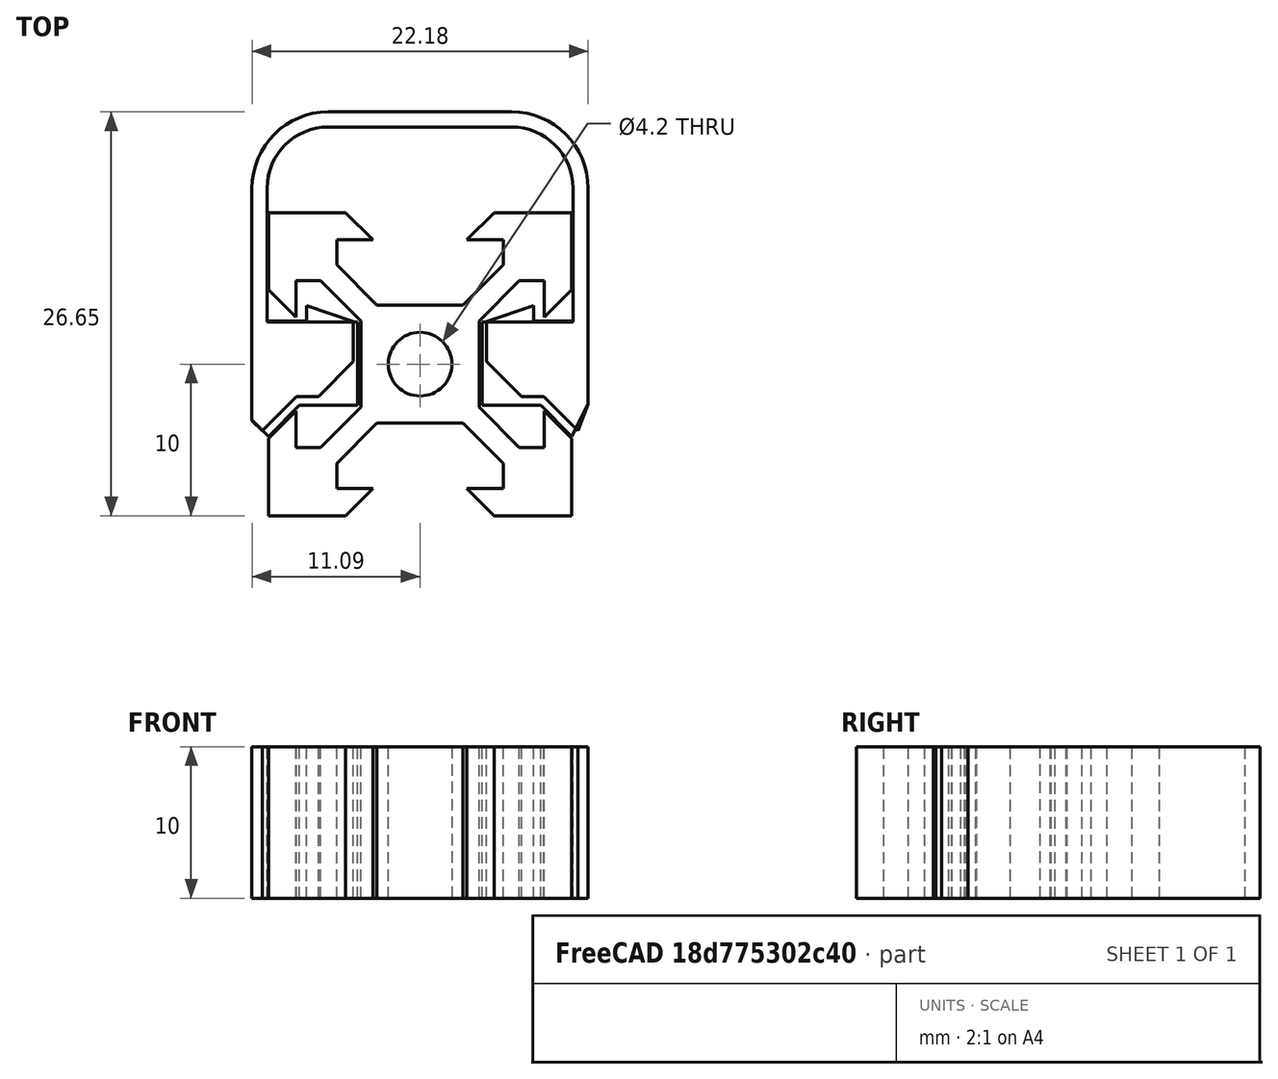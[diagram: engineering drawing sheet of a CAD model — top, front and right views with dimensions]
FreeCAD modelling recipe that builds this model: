
FCSTD DOCUMENT  (FreeCAD 0.21R33694 (Git))
Label: mes_crochets_pour_v_slot
License: All rights reserved
LicenseURL: http://en.wikipedia.org/wiki/All_rights_reserved
objects: Sketcher::SketchObject×3, PartDesign::Pad×2, PartDesign::Body×2, App::Part×2, Part::Extrusion×1
note: 10 computed .brp shape members not serialized (recipe doc carries the construction recipe); baked Part::Feature solids carry a one-line shape summary decoded from their .brp

FEATURE [Sketcher::SketchObject] Sketch
  FullyConstrained = false
  sketch-geometry (49):
    g0: Circle CenterX=0 CenterY=0 CenterZ=0 NormalX=0 NormalY=0 NormalZ=-1 AngleXU=0 Radius=2.1
    g1: LineSegment StartX=-2.84 StartY=3.90066 StartZ=0 EndX=-5.49934 EndY=6.56 EndZ=0
    g2: LineSegment StartX=-5.49934 StartY=6.56 StartZ=0 EndX=-5.49934 EndY=8.2 EndZ=0
    g3: LineSegment StartX=-5.49934 StartY=8.2 StartZ=0 EndX=-3.1 EndY=8.2 EndZ=0
    g4: LineSegment StartX=-3.1 StartY=8.2 StartZ=0 EndX=-4.9 EndY=10 EndZ=0
    g5: LineSegment StartX=-4.9 StartY=10 StartZ=0 EndX=-10 EndY=10 EndZ=0
    g6: LineSegment StartX=-10 StartY=10 StartZ=0 EndX=-10 EndY=4.9 EndZ=0
    g7: LineSegment StartX=-10 StartY=4.9 StartZ=0 EndX=-8.2 EndY=3.1 EndZ=0
    g8: LineSegment StartX=-8.2 StartY=3.1 StartZ=0 EndX=-8.2 EndY=5.49934 EndZ=0
    g9: LineSegment StartX=-8.2 StartY=5.49934 StartZ=0 EndX=-6.56 EndY=5.49934 EndZ=0
    g10: LineSegment StartX=-6.56 StartY=5.49934 StartZ=0 EndX=-3.90066 EndY=2.84 EndZ=0
    g11: LineSegment StartX=-3.90066 StartY=2.84 StartZ=0 EndX=-3.90066 EndY=-1.3e-15 EndZ=0
    g12: LineSegment StartX=-3.90066 StartY=-1.1e-15 StartZ=0 EndX=-3.90066 EndY=-2.84 EndZ=0
    g13: LineSegment StartX=-3.90066 StartY=-2.84 StartZ=0 EndX=-6.56 EndY=-5.49934 EndZ=0
    g14: LineSegment StartX=-6.56 StartY=-5.49934 StartZ=0 EndX=-8.2 EndY=-5.49934 EndZ=0
    g15: LineSegment StartX=-8.2 StartY=-5.49934 StartZ=0 EndX=-8.2 EndY=-3.1 EndZ=0
    g16: LineSegment StartX=-8.2 StartY=-3.1 StartZ=0 EndX=-10 EndY=-4.9 EndZ=0
    g17: LineSegment StartX=-10 StartY=-4.9 StartZ=0 EndX=-10 EndY=-10 EndZ=0
    g18: LineSegment StartX=-10 StartY=-10 StartZ=0 EndX=-4.9 EndY=-10 EndZ=0
    g19: LineSegment StartX=-4.9 StartY=-10 StartZ=0 EndX=-3.1 EndY=-8.2 EndZ=0
    g20: LineSegment StartX=-3.1 StartY=-8.2 StartZ=0 EndX=-5.49934 EndY=-8.2 EndZ=0
    g21: LineSegment StartX=-5.49934 StartY=-8.2 StartZ=0 EndX=-5.49934 EndY=-6.56 EndZ=0
    g22: LineSegment StartX=-5.49934 StartY=-6.56 StartZ=0 EndX=-2.84 EndY=-3.90066 EndZ=0
    g23: LineSegment StartX=-2.84 StartY=-3.90066 StartZ=0 EndX=-4e-16 EndY=-3.90066 EndZ=0
    g24: LineSegment StartX=-6e-16 StartY=-3.90066 StartZ=0 EndX=2.84 EndY=-3.90066 EndZ=0
    g25: LineSegment StartX=2.84 StartY=-3.90066 StartZ=0 EndX=5.49934 EndY=-6.56 EndZ=0
    g26: LineSegment StartX=5.49934 StartY=-6.56 StartZ=0 EndX=5.49934 EndY=-8.2 EndZ=0
    g27: LineSegment StartX=5.49934 StartY=-8.2 StartZ=0 EndX=3.1 EndY=-8.2 EndZ=0
    g28: LineSegment StartX=3.1 StartY=-8.2 StartZ=0 EndX=4.9 EndY=-10 EndZ=0
    g29: LineSegment StartX=4.9 StartY=-10 StartZ=0 EndX=10 EndY=-10 EndZ=0
    g30: LineSegment StartX=10 StartY=-10 StartZ=0 EndX=10 EndY=-4.9 EndZ=0
    g31: LineSegment StartX=10 StartY=-4.9 StartZ=0 EndX=8.2 EndY=-3.1 EndZ=0
    g32: LineSegment StartX=8.2 StartY=-3.1 StartZ=0 EndX=8.2 EndY=-5.49934 EndZ=0
    g33: LineSegment StartX=8.2 StartY=-5.49934 StartZ=0 EndX=6.56 EndY=-5.49934 EndZ=0
    g34: LineSegment StartX=6.56 StartY=-5.49934 StartZ=0 EndX=3.90066 EndY=-2.84 EndZ=0
    g35: LineSegment StartX=3.90066 StartY=-2.84 StartZ=0 EndX=3.90066 EndY=-1.3e-15 EndZ=0
    g36: LineSegment StartX=3.90066 StartY=-1.1e-15 StartZ=0 EndX=3.90066 EndY=2.84 EndZ=0
    g37: LineSegment StartX=3.90066 StartY=2.84 StartZ=0 EndX=6.56 EndY=5.49934 EndZ=0
    g38: LineSegment StartX=6.56 StartY=5.49934 StartZ=0 EndX=8.2 EndY=5.49934 EndZ=0
    g39: LineSegment StartX=8.2 StartY=5.49934 StartZ=0 EndX=8.2 EndY=3.1 EndZ=0
    g40: LineSegment StartX=8.2 StartY=3.1 StartZ=0 EndX=10 EndY=4.9 EndZ=0
    g41: LineSegment StartX=10 StartY=4.9 StartZ=0 EndX=10 EndY=10 EndZ=0
    g42: LineSegment StartX=10 StartY=10 StartZ=0 EndX=4.9 EndY=10 EndZ=0
    g43: LineSegment StartX=4.9 StartY=10 StartZ=0 EndX=3.1 EndY=8.2 EndZ=0
    g44: LineSegment StartX=3.1 StartY=8.2 StartZ=0 EndX=5.49934 EndY=8.2 EndZ=0
    g45: LineSegment StartX=5.49934 StartY=8.2 StartZ=0 EndX=5.49934 EndY=6.56 EndZ=0
    g46: LineSegment StartX=5.49934 StartY=6.56 StartZ=0 EndX=2.84 EndY=3.90066 EndZ=0
    g47: LineSegment StartX=2.84 StartY=3.90066 StartZ=0 EndX=0 EndY=3.90066 EndZ=0
    g48: LineSegment StartX=0 StartY=3.90066 StartZ=0 EndX=-2.84 EndY=3.90066 EndZ=0
FEATURE [Part::Extrusion] Extrude  label="2020"
  Base = -> Sketch
  Dir = (0,0,1)
  DirMode = 2
  FaceMakerClass = Part::FaceMakerBullseye
  LengthFwd = 10
  LengthRev = 0
  Solid = true
  Symmetric = false
FEATURE [Sketcher::SketchObject] Sketch001
  FullyConstrained = false
  MapMode = 5
  Support = -> [XY_Plane001]
  sketch-geometry (20):
    g0: LineSegment StartX=-4.10936 StartY=2.79561 StartZ=0 EndX=-10.0927 EndY=2.79561 EndZ=0
    g1: LineSegment StartX=-10.0927 StartY=2.79561 StartZ=0 EndX=-10.0927 EndY=11.6045 EndZ=0
    g2: LineSegment StartX=-6.04309 StartY=15.6542 StartZ=0 EndX=6.04309 EndY=15.6542 EndZ=0
    g3: LineSegment StartX=10.0927 StartY=11.6045 StartZ=0 EndX=10.0927 EndY=2.79561 EndZ=0
    g4: LineSegment StartX=10.0927 StartY=2.79561 StartZ=0 EndX=4.10936 EndY=2.79561 EndZ=0
    g5: LineSegment StartX=4.10936 StartY=2.79561 StartZ=0 EndX=4.10936 EndY=-2.72232 EndZ=0
    g6: LineSegment StartX=11.0927 StartY=-2.64474 StartZ=0 EndX=11.0927 EndY=11.6045 EndZ=0
    g7: LineSegment StartX=6.04309 StartY=16.6542 StartZ=0 EndX=-6.04309 EndY=16.6542 EndZ=0
    g8: LineSegment StartX=-11.0927 StartY=11.6045 StartZ=0 EndX=-11.0927 EndY=-3.66633 EndZ=0
    g9: LineSegment StartX=-4.10936 StartY=-2.72232 StartZ=0 EndX=-4.10936 EndY=2.79561 EndZ=0
    g10: LineSegment StartX=-4.10936 StartY=-2.72232 StartZ=0 EndX=-7.96016 EndY=-2.72232 EndZ=0
    g11: LineSegment StartX=-7.96016 StartY=-2.72232 StartZ=0 EndX=-9.99845 EndY=-4.76061 EndZ=0
    g12: LineSegment StartX=-9.99845 StartY=-4.76061 StartZ=0 EndX=-11.0927 EndY=-3.66633 EndZ=0
    g13: LineSegment StartX=4.10936 StartY=-2.72232 StartZ=0 EndX=7.96016 EndY=-2.72232 EndZ=0
    g14: LineSegment StartX=7.96016 StartY=-2.72232 StartZ=0 EndX=9.99845 EndY=-4.76061 EndZ=0
    g15: LineSegment StartX=9.99845 StartY=-4.76061 StartZ=0 EndX=11.0927 EndY=-2.64474 EndZ=0
    g16: ArcOfCircle CenterX=-6.04309 CenterY=11.6045 CenterZ=0 NormalX=0 NormalY=0 NormalZ=1 AngleXU=0 Radius=4.04964 StartAngle=1.5708 EndAngle=3.14159
    g17: ArcOfCircle CenterX=-6.04309 CenterY=11.6045 CenterZ=0 NormalX=0 NormalY=0 NormalZ=1 AngleXU=0 Radius=5.04964 StartAngle=1.5708 EndAngle=3.14159
    g18: ArcOfCircle CenterX=6.04309 CenterY=11.6045 CenterZ=0 NormalX=0 NormalY=0 NormalZ=1 AngleXU=0 Radius=4.04964 StartAngle=0 EndAngle=1.5708
    g19: ArcOfCircle CenterX=6.04309 CenterY=11.6045 CenterZ=0 NormalX=0 NormalY=0 NormalZ=1 AngleXU=0 Radius=5.04964 StartAngle=0 EndAngle=1.5708
  constraints (39):
    c: Horizontal(g0)
    c: Coincident(g0,g1)
    c: Vertical(g1)
    c: Coincident(g3,g4)
    c: Coincident(g4,g5)
    c: Vertical(g6)
    c: Vertical(g8)
    c: Coincident(g9,g0)
    c: Vertical(g9)
    c: Symmetric(g13,g9,g-2)
    c: Symmetric(g4,g0,g-2)
    c: Symmetric(g3,g0,g-2)
    c: Coincident(g10,g9)
    c: Coincident(g11,g10)
    c: Coincident(g12,g11)
    c: Coincident(g12,g8)
    c: Horizontal(g13)
    c: Coincident(g15,g6)
    c: Symmetric(g10,g13,g-2)
    c: Symmetric(g14,g11,g-2)
    c: Angle(g11) = -2.35619
    c: Angle(g12) = 2.35619
    c: Coincident(g13,g5)
    c: Tangent(g1,g16) = 1.5708
    c: Tangent(g2,g16) = 1.5708
    c: Tangent(g8,g17) = -1.5708
    c: Tangent(g7,g17) = -1.5708
    c: Horizontal(g7)
    c: Tangent(g2,g18) = 1.5708
    c: Tangent(g3,g18) = 1.5708
    c: Horizontal(g2)
    c: Tangent(g6,g19) = -1.5708
    c: Tangent(g7,g19) = -1.5708
    c: Coincident(g16,g17)
    c: Coincident(g19,g18)
    c: Symmetric(g18,g16,g-2)
    c: DistanceX(g8,g0) = 1
    c: Coincident(g14,g13)
    c: Coincident(g15,g14)
FEATURE [PartDesign::Pad] Pad
  Direction = (0,0,1)
  Length = 10
  Length2 = 10
  Profile = -> Sketch001
  ReferenceAxis = -> Sketch001 [N_Axis]
  Type = 0
FEATURE [PartDesign::Body] Body
  Group = -> [Sketch001,Pad]
  Origin = -> Origin001
  Tip = -> Pad
FEATURE [App::Part] Part  label="crochet_v1"
  Group = -> [Body]
  Origin = -> Origin
FEATURE [Sketcher::SketchObject] Sketch002
  FullyConstrained = false
  MapMode = 5
  Support = -> [XY_Plane003]
  sketch-geometry (29):
    g0: LineSegment StartX=-10.0911 StartY=2.8532 StartZ=0 EndX=-10.0911 EndY=11.6048 EndZ=0
    g1: LineSegment StartX=-6.04231 StartY=15.6536 StartZ=0 EndX=6.04231 EndY=15.6536 EndZ=0
    g2: LineSegment StartX=10.0911 StartY=11.6048 StartZ=0 EndX=10.0911 EndY=2.8532 EndZ=0
    g3: LineSegment StartX=11.0911 StartY=-2.64474 StartZ=0 EndX=11.0911 EndY=11.6048 EndZ=0
    g4: LineSegment StartX=6.04231 StartY=16.6536 StartZ=0 EndX=-6.04231 EndY=16.6536 EndZ=0
    g5: LineSegment StartX=-11.0911 StartY=11.6048 StartZ=0 EndX=-11.0911 EndY=-3.7116 EndZ=0
    g6: LineSegment StartX=-8.152 StartY=-2.12794 StartZ=0 EndX=-10.4134 EndY=-4.38933 EndZ=0
    g7: LineSegment StartX=-10.4134 StartY=-4.38933 StartZ=0 EndX=-11.0911 EndY=-3.7116 EndZ=0
    g8: LineSegment StartX=6.69807 StartY=-2.12794 StartZ=0 EndX=8.152 EndY=-2.12794 EndZ=0
    g9: LineSegment StartX=8.152 StartY=-2.12794 StartZ=0 EndX=10.4134 EndY=-4.38933 EndZ=0
    g10: LineSegment StartX=10.4134 StartY=-4.38933 StartZ=0 EndX=11.0911 EndY=-2.64474 EndZ=0
    g11: ArcOfCircle CenterX=-6.04231 CenterY=11.6048 CenterZ=0 NormalX=0 NormalY=0 NormalZ=1 AngleXU=0 Radius=4.0488 StartAngle=1.5708 EndAngle=3.14159
    g12: ArcOfCircle CenterX=-6.04231 CenterY=11.6048 CenterZ=0 NormalX=0 NormalY=0 NormalZ=1 AngleXU=0 Radius=5.0488 StartAngle=1.5708 EndAngle=3.14159
    g13: ArcOfCircle CenterX=6.04231 CenterY=11.6048 CenterZ=0 NormalX=0 NormalY=0 NormalZ=1 AngleXU=0 Radius=4.0488 StartAngle=0 EndAngle=1.5708
    g14: ArcOfCircle CenterX=6.04231 CenterY=11.6048 CenterZ=0 NormalX=0 NormalY=0 NormalZ=1 AngleXU=0 Radius=5.0488 StartAngle=0 EndAngle=1.5708
    g15: LineSegment StartX=-4.4 StartY=2.8 StartZ=0 EndX=-4.4 EndY=0.170135 EndZ=0
    g16: LineSegment StartX=-4.4 StartY=0.170135 StartZ=0 EndX=-6.69807 EndY=-2.12794 EndZ=0
    g17: LineSegment StartX=-8.152 StartY=-2.12794 StartZ=0 EndX=-6.69807 EndY=-2.12794 EndZ=0
    g18: LineSegment StartX=4.4 StartY=2.8 StartZ=0 EndX=4.4 EndY=0.170135 EndZ=0
    g19: LineSegment StartX=4.4 StartY=0.170135 StartZ=0 EndX=6.69807 EndY=-2.12794 EndZ=0
    g20: GeomPoint X=-17.854 Y=3.90157 Z=0
    g21: GeomPoint X=7.48528 Y=2.8532 Z=0
    g22: GeomPoint X=7.48528 Y=3.8532 Z=0
    g23: LineSegment StartX=4.4 StartY=2.8 StartZ=0 EndX=7.48528 EndY=3.8532 EndZ=0
    g24: LineSegment StartX=7.48528 StartY=2.8532 StartZ=0 EndX=7.48528 EndY=3.8532 EndZ=0
    g25: LineSegment StartX=7.48528 StartY=2.8532 StartZ=0 EndX=10.0911 EndY=2.8532 EndZ=0
    g26: LineSegment StartX=-10.0911 StartY=2.8532 StartZ=0 EndX=-7.48528 EndY=2.8532 EndZ=0
    g27: LineSegment StartX=-7.48528 StartY=2.8532 StartZ=0 EndX=-7.48528 EndY=3.8532 EndZ=0
    g28: LineSegment StartX=-7.48528 StartY=3.8532 StartZ=0 EndX=-4.4 EndY=2.8 EndZ=0
  constraints (58):
    c: Vertical(g0)
    c: Vertical(g3)
    c: Vertical(g5)
    c: Symmetric(g18,g15,g-2)
    c: Symmetric(g2,g0,g-2)
    c: Coincident(g7,g6)
    c: Coincident(g7,g5)
    c: Horizontal(g8)
    c: Coincident(g10,g3)
    c: Symmetric(g6,g8,g-2)
    c: Symmetric(g9,g6,g-2)
    c: Angle(g6) = -2.35619
    c: Angle(g7) = 2.35619
    c: Tangent(g0,g11) = 1.5708
    c: Tangent(g1,g11) = 1.5708
    c: Tangent(g5,g12) = -1.5708
    c: Tangent(g4,g12) = -1.5708
    c: Horizontal(g4)
    c: Tangent(g1,g13) = 1.5708
    c: Tangent(g2,g13) = 1.5708
    c: Horizontal(g1)
    c: Tangent(g3,g14) = -1.5708
    c: Tangent(g4,g14) = -1.5708
    c: Coincident(g11,g12)
    c: Coincident(g14,g13)
    c: Symmetric(g13,g11,g-2)
    c: DistanceX(g5,g0) = 1
    c: Coincident(g9,g8)
    c: Coincident(g10,g9)
    c: Vertical(g15)
    c: Coincident(g16,g15)
    c: Coincident(g17,g6)
    c: Coincident(g17,g16)
    c: Horizontal(g17)
    c: Vertical(g18)
    c: Coincident(g18,g19)
    c: Coincident(g19,g8)
    c: Angle(g16) = -2.35619
    c: DistanceX(g15,g-1) = 4.4
    c: DistanceY(g-1,g18) = 2.8
    c: Coincident(g23,g18)
    c: Coincident(g23,g22)
    c: Coincident(g24,g21)
    c: Coincident(g24,g23)
    c: Coincident(g25,g24)
    c: Coincident(g25,g2)
    c: Vertical(g24)
    c: Horizontal(g25)
    c: Coincident(g0,g26)
    c: Coincident(g26,g27)
    c: Coincident(g27,g28)
    c: Coincident(g28,g15)
    c: Vertical(g27)
    c: Horizontal(g26)
    c: Symmetric(g27,g23,g-2)
    c: DistanceY(g26,g27) = 1
    c: Horizontal(g15,g18)
    c: Angle(g19) = -0.785398
FEATURE [PartDesign::Pad] Pad001
  Direction = (0,0,1)
  Length = 10
  Length2 = 10
  Profile = -> Sketch002
  ReferenceAxis = -> Sketch002 [N_Axis]
  Type = 0
FEATURE [PartDesign::Body] Body001
  Group = -> [Sketch002,Pad001]
  Origin = -> Origin003
  Tip = -> Pad001
FEATURE [App::Part] Part001  label="crochet_v2"
  Group = -> [Body001]
  Origin = -> Origin002
